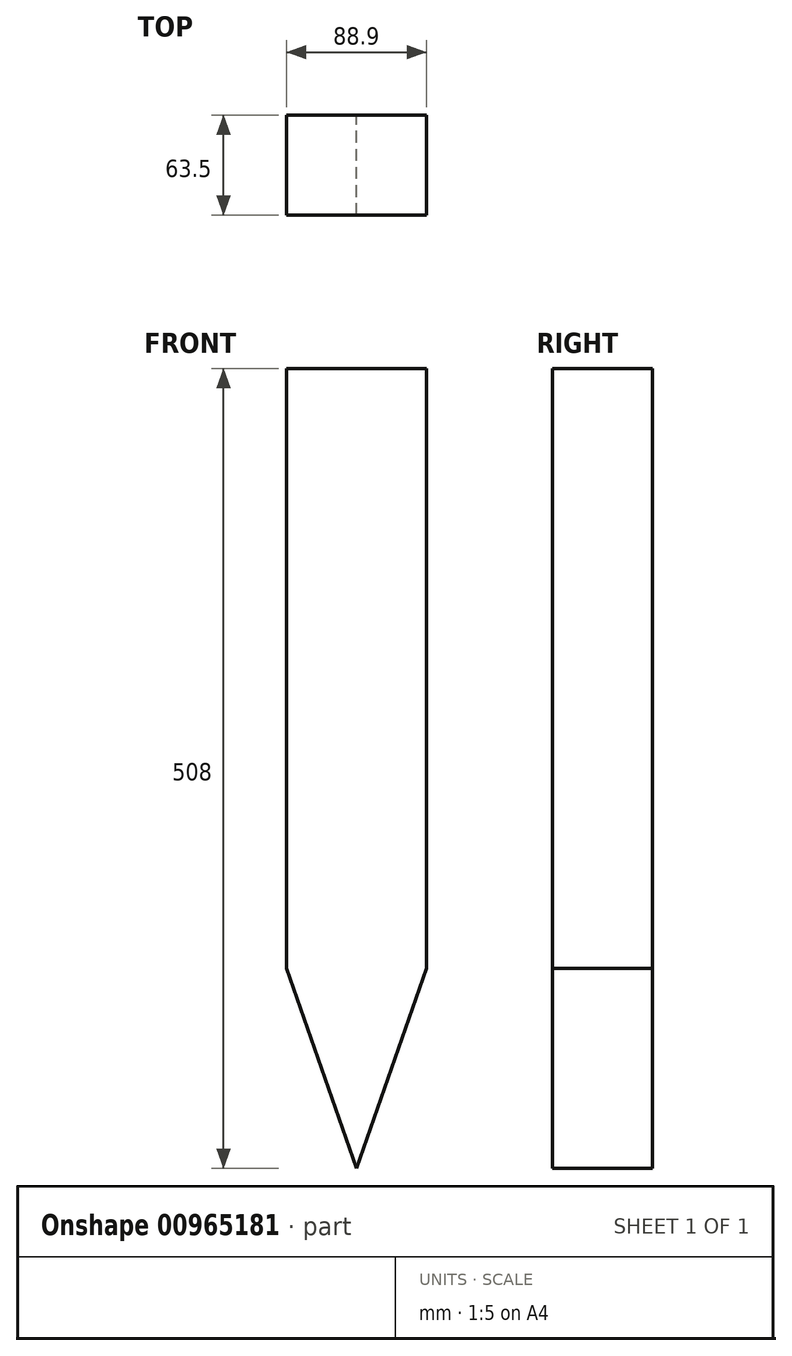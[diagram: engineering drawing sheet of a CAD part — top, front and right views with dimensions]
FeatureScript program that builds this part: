
annotation { "Feature Type Name" : "Feature", "Feature Type Description" : "" }
export const myFeature = defineFeature(function(context is Context, id is Id, definition is map)
    precondition{}
    {
        {
            var Q0;
            Q0=qCreatedBy(makeId("Top.planeOp"),FACE);
            var sketch = newSketch(context, id + "F0", { "sketchPlane" : qUnion([Q0])});
            skLineSegment(sketch, "E0.bottom", {"start": v(-306.38, -66.73) * mm, "end": v(-217.48, -66.73) * mm});
            skLineSegment(sketch, "E0.top", {"start": v(-306.38, -28.63) * mm, "end": v(-217.48, -28.63) * mm});
            skLineSegment(sketch, "E0.left", {"start": v(-306.38, -66.73) * mm, "end": v(-306.38, -28.63) * mm});
            skLineSegment(sketch, "E0.right", {"start": v(-217.48, -66.73) * mm, "end": v(-217.48, -28.63) * mm});
            skSolve(sketch);
        }
        {
            var Q0;
            Q0=makeQuery(id+"F0.imprint","IMPRINT",FACE,{"disambiguationData":[TD([[makeQuery(id+"F0.imprint","IMPRINT",EDGE,{"derivedFrom":sQuery(id+"F0.wireOp",EDGE,"E0.bottom")}),1.0]])]});
            extrude(context, id + "F1", {"entities" : qUnion([Q0]), "depth" : 508 * mm, "offsetDistance" : 25.4 * mm});
        }
        {
            var Q0;
            Q0=makeQuery(id+"F1.opExtrude","SWEPT_FACE",FACE,{"disambiguationData":[OSD([sQuery(id+"F0.wireOp",EDGE,"E0.bottom")])]});
            var sketch = newSketch(context, id + "F2", { "sketchPlane" : qUnion([Q0])});
            skLineSegment(sketch, "E1", {"start": v(-217.48, 127) * mm, "end": v(-306.38, 127) * mm, "construction": true});
            skLineSegment(sketch, "E2", {"start": v(-306.38, 127) * mm, "end": v(-261.93, 0) * mm});
            skLineSegment(sketch, "E3", {"start": v(-261.93, 0) * mm, "end": v(-217.48, 127) * mm});
            skSolve(sketch);
        }
        {
            var Q0;
            {var subQ3=sQuery(id+"F2.wireOp",EDGE,"E2");Q0=makeQuery(id+"F2.imprint","IMPRINT",FACE,{"disambiguationData":[TD([[makeQuery(id+"F2.imprint","IMPRINT",EDGE,{"derivedFrom":subQ3}),1.0]])]});}
            extrude(context, id + "F3", {"entities" : qUnion([Q0]), "operationType" : NewBodyOperationType.ADD, "depth" : 25.4 * mm, "offsetDistance" : 25.4 * mm});
        }
        {
            var Q0;
            {var subQ0=sQuery(id+"F0.wireOp",EDGE,"E0.left");var subQ1=sQuery(id+"F0.wireOp",EDGE,"E0.bottom");var subQ2=makeQuery(id+"F1.opExtrude","SWEPT_FACE",FACE,{"disambiguationData":[OSD([subQ1])]});Q0=makeQuery(id+"F3.boolean.opBoolean","SPLIT",FACE,{"disambiguationData":[TD([makeQuery(id+"F1.opExtrude","SWEPT_FACE",FACE,{"disambiguationData":[OSD([subQ0])]})])],"derivedFrom":subQ2});}
            var Q1;
            {var subQ0=sQuery(id+"F0.wireOp",EDGE,"E0.right");var subQ1=sQuery(id+"F0.wireOp",EDGE,"E0.bottom");var subQ2=makeQuery(id+"F1.opExtrude","SWEPT_FACE",FACE,{"disambiguationData":[OSD([subQ1])]});Q1=makeQuery(id+"F3.boolean.opBoolean","SPLIT",FACE,{"disambiguationData":[TD([makeQuery(id+"F1.opExtrude","SWEPT_FACE",FACE,{"disambiguationData":[OSD([subQ0])]})])],"derivedFrom":subQ2});}
            extrude(context, id + "F4", {"entities" : qUnion([Q0, Q1]), "operationType" : NewBodyOperationType.REMOVE, "endBound" : BoundingType.THROUGH_ALL, "oppositeDirection" : true, "depth" : 25.4 * mm, "offsetDistance" : 25.4 * mm});
        }
    });
